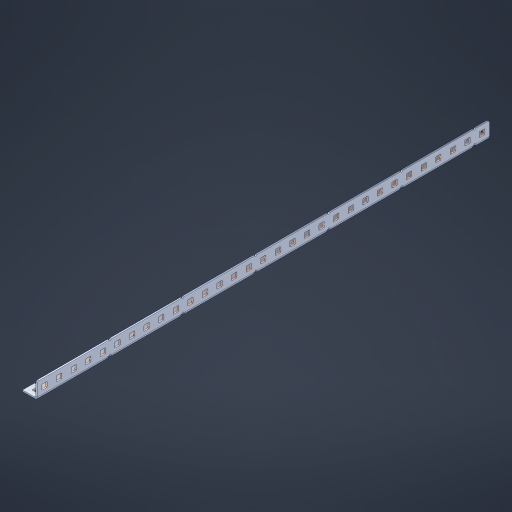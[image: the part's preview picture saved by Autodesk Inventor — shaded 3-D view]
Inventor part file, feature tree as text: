
AUTODESK INVENTOR PART (.ipt)
format: ipt  version: 2023 (Build 270158000, 158)  size: 1,244,672 bytes
history: native  units: in
note: dims shown in document units (in); Inventor stores cm internally (conversion verified against a paired STEP export)
features: other x100, extrude x91, sheet_metal_op x11, sketch x10, pattern_linear x2, mirror x1, chamfer x1
ambient origin geometry x8: Origin, YZ Plane, XZ Plane, XY Plane, X Axis, Y Axis, Z Axis, Center Point
bodies: Solid1 (feature_tree), Body (feature_tree)
feature tree (216):
  sheet_metal_op  "Flanges"
  other  "Flange Pattern Plane"
  other  "Flange Pattern Sketch"
  sheet_metal_op  "Flange Pattern"
  sheet_metal_op  "Body Pattern"
  pattern_linear  "Center Pattern"  Spacing1=0.0469in  [1 undecoded]
  other  "Arc Length"
  mirror  "Notch Mirror"
  pattern_linear  "Notch Pattern"  Spacing1=0.182in  [1 undecoded]
  chamfer  "End Chamfer"
  extrude  "Half Cut"  Depth=0.02in
  sketch  "Sketch1"  dims[d0=1.0in]
  other  "Plate1"
  sketch  "Sketch2"  dims[d1=15.5in]
  other  "Plate2"
  sheet_metal_op  "Bend1"
  sheet_metal_op  "Corner1"
  sketch  "Sketch3"  dims[d2=0.0469in]
  sketch  "Sketch7"  dims[d3=0.0469in]
  other  "Srf1"
  other  "Srf2"
  sketch  "Sketch8"  dims[d4=0.0234in]
  sketch  "Sketch9"  dims[d5=0.0938in]
  other  "Srf91"
  sheet_metal_op  "Body Pattern Sketch"
  other  "Srf92"
  sketch  "Sketch13"  dims[d6=0.0469in]
  sketch  "Sketch14"  dims[d7=0.5in d8=90.0deg d9=0.0312in]
  sketch  "Sketch15"  dims[d10=0.1875in]
  sketch  "Sketch16"  dims[d11=0.0469in d12=0.0469in d16=0.182in d17=0.02in d18=0.0469in d19=0.0in d20=0.25in d21=0.25in d38=12.2047in d40=0.5in d41=0.3937in d43=1.0in d46=0.172in d47=1.0in d48=0.0in d49=0.182in d50=0.02in d51=0.25in d52=0.25in d53=0.0469in d54=0.0in d55=0.172in d56=1.0in d57=0.0in d58=0.25in d60=12.2047in d62=0.5in d63=0.3937in d65=0.5in d85=0.1227in d86=0.1659in d88=0.04in d89=0.0469in d90=0.0in d91=0.04in d92=0.0491in d95=2.5in d96=0.04in d97=0.25in d98=45.0deg d99=0.25in d100=0.5in d101=0.0in d102=2.497in d106=0.182in d107=0.02in d108=0.5in d109=0.5in d110=0.0469in d111=0.0in d112=0.172in d113=0.5in d114=0.0in d117=0.5in d118=0.5in d119=0.5in]
  other  "Srf786"
  other  "Srf823"
  other  "Srf824"
  other  "Srf825"
  other  "Srf826"
  other  "Srf827"
  other  "Srf828"
  other  "Srf829"
  other  "Srf856"
  other  "Srf857"
  other  "Srf858"
  other  "Srf859"
  other  "Srf860"
  other  "Srf861"
  other  "Srf862"
  other  "Srf889"
  other  "Srf890"
  other  "Srf891"
  other  "Srf892"
  other  "Srf893"
  other  "Srf894"
  other  "Srf895"
  other  "Srf896"
  other  "Srf922"
  other  "Srf923"
  other  "Srf924"
  other  "Srf925"
  other  "Srf926"
  other  "Srf959"
  other  "Srf960"
  other  "Srf961"
  other  "Srf962"
  other  "Srf963"
  other  "Srf996"
  other  "Srf997"
  other  "Srf998"
  other  "Srf999"
  other  "Srf1000"
  other  "Srf1143"
  other  "Srf1144"
  other  "Srf1145"
  other  "Srf1146"
  other  "Srf1147"
  other  "Srf1148"
  other  "Srf1149"
  other  "Srf1150"
  other  "Srf1151"
  other  "Srf1152"
  other  "Srf1153"
  other  "Srf1154"
  other  "Srf1155"
  other  "Srf1156"
  other  "Srf1157"
  other  "Srf1158"
  other  "Srf1159"
  other  "Srf1199"
  other  "Srf1200"
  other  "Srf1201"
  other  "Srf1202"
  other  "Srf1203"
  other  "Srf1204"
  other  "Srf1205"
  other  "Srf1206"
  other  "Srf1207"
  other  "Srf1208"
  other  "Srf1209"
  other  "Srf1210"
  other  "Srf1211"
  other  "Srf1212"
  other  "Srf1213"
  other  "Srf1214"
  other  "Srf1215"
  other  "Srf1255"
  other  "Srf1256"
  other  "Srf1257"
  other  "Srf1258"
  other  "Srf1259"
  other  "Srf1260"
  other  "Srf1261"
  other  "Srf1262"
  other  "Srf1263"
  other  "Srf1264"
  other  "Srf1265"
  other  "Srf1266"
  other  "Srf1267"
  other  "Srf1268"
  other  "Srf1269"
  other  "Srf1270"
  other  "Srf1271"
  sheet_metal_op  "Flange Stamp"
  sheet_metal_op  "Flange Circle"
  sheet_metal_op  "Body Stamp"
  sheet_metal_op  "Body Circle"
  other  "Center Stamp"
  other  "Center Circle"
  sheet_metal_op  "Notch"
  extrude  "ExtrusionSrf2"  Depth=0.0469in
  extrude  "ExtrusionSrf92"  TaperAngle=0.0deg  [1 undecoded]
  extrude  "ExtrusionSrf823"  Depth=0.5in
  extrude  "ExtrusionSrf824"  Depth=0.5in
  extrude  "ExtrusionSrf825"  Depth=0.5in
  extrude  "ExtrusionSrf826"  Depth=0.5in
  extrude  "ExtrusionSrf827"  Depth=1.0in TaperAngle=0.0deg
  extrude  "ExtrusionSrf828"  Depth=0.182in
  extrude  "ExtrusionSrf829"  Depth=0.02in
  extrude  "ExtrusionSrf856"  Depth=0.5in
  extrude  "ExtrusionSrf857"  Depth=0.5in
  extrude  "ExtrusionSrf858"  Depth=0.0469in
  extrude  "ExtrusionSrf859"  TaperAngle=0.0deg  [1 undecoded]
  extrude  "ExtrusionSrf860"  Depth=0.5in
  extrude  "ExtrusionSrf861"  Depth=1.0in TaperAngle=0.0deg
  extrude  "ExtrusionSrf862"  Depth=0.5in
  extrude  "ExtrusionSrf889"  Depth=0.5in
  extrude  "ExtrusionSrf890"  Depth=0.5in
  extrude  "ExtrusionSrf891"  Depth=0.5in
  extrude  "ExtrusionSrf892"  Depth=0.5in
  extrude  "ExtrusionSrf893"  Depth=0.5in
  extrude  "ExtrusionSrf894"  Depth=0.0469in
  extrude  "ExtrusionSrf895"  TaperAngle=0.0deg  [1 undecoded]
  extrude  "ExtrusionSrf896"  Depth=0.5in
  extrude  "ExtrusionSrf922"  Depth=0.5in
  extrude  "ExtrusionSrf923"  Depth=0.5in
  extrude  "ExtrusionSrf924"  Depth=0.5in TaperAngle=45.0deg
  extrude  "ExtrusionSrf925"  Depth=0.5in
  extrude  "ExtrusionSrf926"  Depth=0.5in TaperAngle=0.0deg
  extrude  "ExtrusionSrf959"  Depth=0.5in
  extrude  "ExtrusionSrf960"  Depth=0.182in
  extrude  "ExtrusionSrf961"  Depth=0.02in
  extrude  "ExtrusionSrf962"  Depth=0.5in
  extrude  "ExtrusionSrf963"  Depth=0.5in
  extrude  "ExtrusionSrf996"  Depth=0.0469in
  extrude  "ExtrusionSrf997"  TaperAngle=0.0deg  [1 undecoded]
  extrude  "ExtrusionSrf998"  Depth=0.5in
  extrude  "ExtrusionSrf999"  Depth=0.5in TaperAngle=0.0deg
  extrude  "ExtrusionSrf1000"  Depth=0.5in
  extrude  "ExtrusionSrf1143"  Depth=0.5in
  extrude  "ExtrusionSrf1144"  Depth=0.5in
  extrude  "ExtrusionSrf1145"  [1 undecoded]
  extrude  "ExtrusionSrf1146"  [1 undecoded]
  extrude  "ExtrusionSrf1147"  [1 undecoded]
  extrude  "ExtrusionSrf1148"  [1 undecoded]
  extrude  "ExtrusionSrf1149"  [1 undecoded]
  extrude  "ExtrusionSrf1150"  [1 undecoded]
  extrude  "ExtrusionSrf1151"  [1 undecoded]
  extrude  "ExtrusionSrf1152"  [1 undecoded]
  extrude  "ExtrusionSrf1153"  [1 undecoded]
  extrude  "ExtrusionSrf1154"  [1 undecoded]
  extrude  "ExtrusionSrf1155"  [1 undecoded]
  extrude  "ExtrusionSrf1156"  [1 undecoded]
  extrude  "ExtrusionSrf1157"  [1 undecoded]
  extrude  "ExtrusionSrf1158"  [1 undecoded]
  extrude  "ExtrusionSrf1159"  [1 undecoded]
  extrude  "ExtrusionSrf1199"  [1 undecoded]
  extrude  "ExtrusionSrf1200"  [1 undecoded]
  extrude  "ExtrusionSrf1201"  [1 undecoded]
  extrude  "ExtrusionSrf1202"  [1 undecoded]
  extrude  "ExtrusionSrf1203"  [1 undecoded]
  extrude  "ExtrusionSrf1204"  [1 undecoded]
  extrude  "ExtrusionSrf1205"  [1 undecoded]
  extrude  "ExtrusionSrf1206"  [1 undecoded]
  extrude  "ExtrusionSrf1207"  [1 undecoded]
  extrude  "ExtrusionSrf1208"  [1 undecoded]
  extrude  "ExtrusionSrf1209"  [1 undecoded]
  extrude  "ExtrusionSrf1210"  [1 undecoded]
  extrude  "ExtrusionSrf1211"  [1 undecoded]
  extrude  "ExtrusionSrf1212"  [1 undecoded]
  extrude  "ExtrusionSrf1213"  [1 undecoded]
  extrude  "ExtrusionSrf1214"  [1 undecoded]
  extrude  "ExtrusionSrf1215"  [1 undecoded]
  extrude  "ExtrusionSrf1255"  [1 undecoded]
  extrude  "ExtrusionSrf1256"  [1 undecoded]
  extrude  "ExtrusionSrf1257"  [1 undecoded]
  extrude  "ExtrusionSrf1258"  [1 undecoded]
  extrude  "ExtrusionSrf1259"  [1 undecoded]
  extrude  "ExtrusionSrf1260"  [1 undecoded]
  extrude  "ExtrusionSrf1261"  [1 undecoded]
  extrude  "ExtrusionSrf1262"  [1 undecoded]
  extrude  "ExtrusionSrf1263"  [1 undecoded]
  extrude  "ExtrusionSrf1264"  [1 undecoded]
  extrude  "ExtrusionSrf1265"  [1 undecoded]
  extrude  "ExtrusionSrf1266"  [1 undecoded]
  extrude  "ExtrusionSrf1267"  [1 undecoded]
  extrude  "ExtrusionSrf1268"  [1 undecoded]
  extrude  "ExtrusionSrf1269"  [1 undecoded]
  extrude  "ExtrusionSrf1270"  [1 undecoded]
  extrude  "ExtrusionSrf1271"  [1 undecoded]
note: 55 required parameter values undecoded (feature->parameter linkage not recoverable at this tier; creation-order binding heuristic only, values carry confidence <= 0.55)
